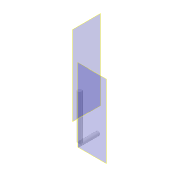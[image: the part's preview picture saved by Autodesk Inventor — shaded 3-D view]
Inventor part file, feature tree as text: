
AUTODESK INVENTOR PART (.ipt)
format: ipt  version: 2019.4 (Build 234330000, 330)  size: 120,320 bytes
history: native  units: mm
features: other x5, sketch x4, reference x4, plane x2, extrude x2, projected_geometry x2, sweep x1
ambient origin geometry x8: Origin, YZ Plane, XZ Plane, XY Plane, X Axis, Y Axis, Z Axis, Center Point
bodies: Solid1 (feature_tree)
feature tree (20):
  plane  "Work Plane1"
  sketch  "Sketch1"  dims[d0=25.0mm d1=63.0mm]
  plane  "Work Plane2"
  sweep  "Sweep1"
  extrude  "Extrusion1"  TaperAngle=45.0deg  [1 undecoded]
  extrude  "Extrusion2"  Depth=10.0mm TaperAngle=0.0deg
  reference  "Reference1"
  reference  "Reference2"
  reference  "Reference3"
  sketch  "Sketch2"  dims[d2=0.0mm d3=0.0mm d4=45.0deg]
  reference  "Reference4"
  sketch  "Sketch3"  dims[d5=10.0mm d6=0.0mm d7=10.0mm d8=0.0mm]
  projected_geometry  "Projected Loop1"
  projected_geometry  "Projected Loop2"
  sketch  "Sketch4"
  other  "Assembly_Opentrons_Autofocus_v1.iam"
  other  "20_focus_inlet_linearflexure_objective_mount_v0:1"
  other  "Assembly_Autofocus_10x_laser_espcam_v1:1"
  other  "20_focus_inlet_linearflexure_motorized_v4:1"
  other  "01_Slide_camera_x_v1:1"
note: 1 required parameter value undecoded (feature->parameter linkage not recoverable at this tier; creation-order binding heuristic only, values carry confidence <= 0.55)
